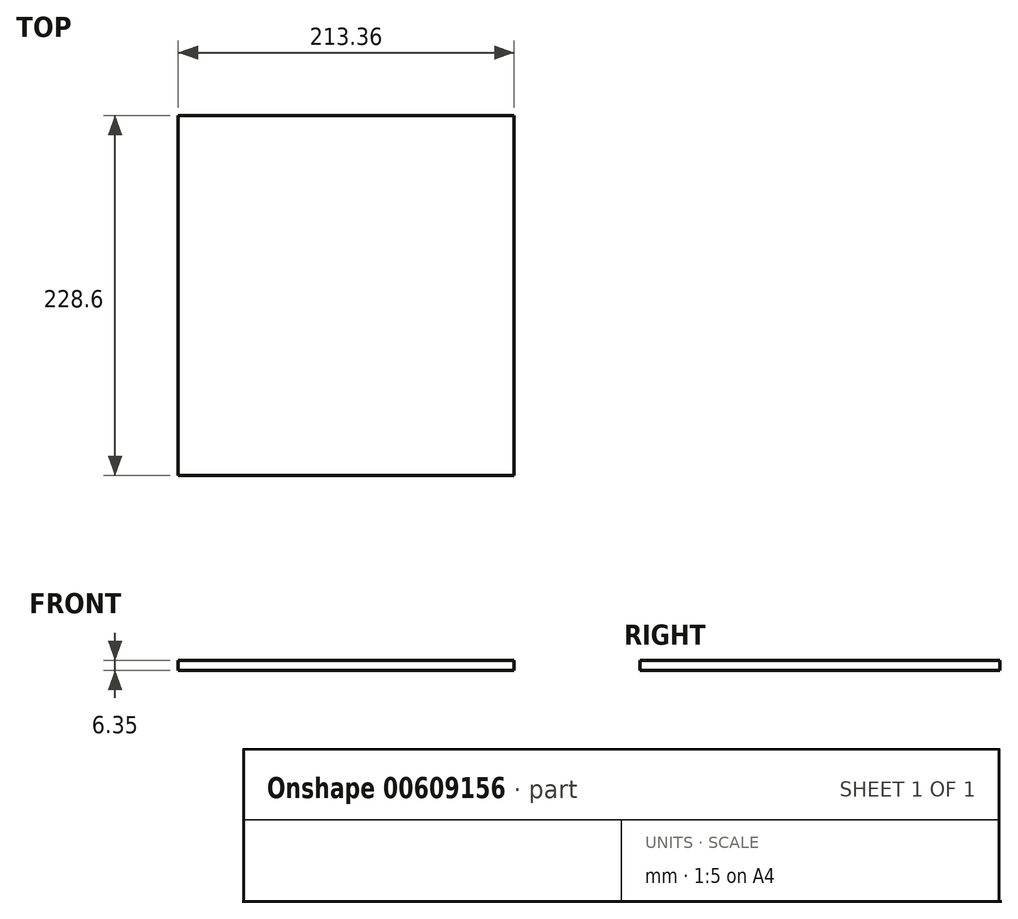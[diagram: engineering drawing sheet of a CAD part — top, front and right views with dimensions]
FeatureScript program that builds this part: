
annotation { "Feature Type Name" : "Feature", "Feature Type Description" : "" }
export const myFeature = defineFeature(function(context is Context, id is Id, definition is map)
    precondition{}
    {
        {
            var Q0;
            Q0=qCreatedBy(makeId("Top.planeOp"),FACE);
            var sketch = newSketch(context, id + "F0", { "sketchPlane" : qUnion([Q0])});
            skLineSegment(sketch, "E0.bottom", {"start": v(0, 0) * mm, "end": v(213.36, 0) * mm});
            skLineSegment(sketch, "E0.top", {"start": v(0, 228.6) * mm, "end": v(213.36, 228.6) * mm});
            skLineSegment(sketch, "E0.left", {"start": v(0, 0) * mm, "end": v(0, 228.6) * mm});
            skLineSegment(sketch, "E0.right", {"start": v(213.36, 0) * mm, "end": v(213.36, 228.6) * mm});
            skSolve(sketch);
        }
        {
            var Q0;
            Q0=makeQuery(id+"F0.imprint","IMPRINT",FACE,{"disambiguationData":[TD([[makeQuery(id+"F0.imprint","IMPRINT",EDGE,{"derivedFrom":sQuery(id+"F0.wireOp",EDGE,"E0.bottom")}),1.0]])]});
            extrude(context, id + "F1", {"entities" : qUnion([Q0]), "depth" : 6.35 * mm, "offsetDistance" : 25.4 * mm});
        }
    });
